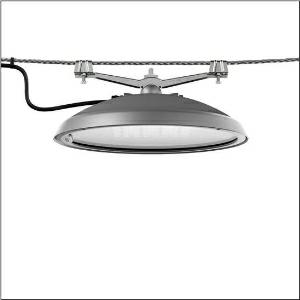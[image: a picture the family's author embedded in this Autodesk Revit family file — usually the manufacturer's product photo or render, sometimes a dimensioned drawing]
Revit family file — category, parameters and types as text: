
# Revit family: dl_r__50_iq_mini___p1_0s_5xa248u41f08fe_3d02
name_source: partatom
category: Lighting Fixtures
units: mm (PartAtom-declared; Revit-internal decimal feet)

## family parameters
Cut with Voids When Loaded = No
Host = Face
Light Source = No
Part Type = Normal
Room Calculation Point = No
Round Connector Dimension = Use Diameter
Shared = No

## types (1)
- --- (1 x LED, 2610 lm, 15.7 W, 4000K)
    Apparent Load = 16 VA
    CIE Flux Codes = 23 54 93 100 100
    Color Rendering = 70
    Color Temperature = 4000K
    Default Elevation = 1800 mm
    Description = DL® 50 iQ mini, catenary luminaire, primary light control with lens, of PMMA, primary optical cover: cover, of toughened safety glass, transparent, light distribution: P1.0s, light emission: direct distribution, primary light characteristic: symmetric, installation type: suspended mounting, LED, High Power LED, rated luminous flux: 2.610lm, luminous efficacy: 166lm/W, light colour: 740, colour temperature: 4000K, control gear: iQ Street-Remote, control: optimised constant luminous flux control (CLO 2.0), Desk-Remote (wireless, voltage-free reading and setting of iQ features in the workshop via application-optimized NFC function/RFID function), Light-Fading, Smart-Wire, Night-Set, Lumen-Switch, Temp-Guard, Auto-Match, Street-Remote, mains connection: 230..240V, AC, 50/60Hz, start of lifetime: 16W, end of service life: 16W, reduction: 8W, luminaire housing, of diecast aluminium, powder-coated, Siteco® metallic grey (DB 702S), diameter: 500mm, height: 115mm, mounting height: 4..12m, protection rating (complete): IP66, insulation class (complete): insulation class II (safety insulation), certification: CE, ENEC, ENEC+, VDE, impact resistance: IK08, permissible operating ambient temperature for outdoor applications: -25..+40°C, standard-compliant lighting for roads and squares, packaging unit: 1 piece

Light Distribution: P1.0s
    Height = 124 mm  [stored 0.406824 ft]
    Lamp = 1 x LED
    Lamp Light Flux = 2610 lm
    Lamp Power = 15.7 W
    Lamp count = 1
    Length = 500 mm
    Luminous efficacy = 166 lm/W
    Manufacturer = Siteco
    ModVariant = No
    Model = 5XA248U41F08FE
    Number of Poles = 1
    OnlyDefault = Yes
    Power Factor = 1
    Product Name = DL® 50 iQ mini | P1.0s
    Product group = catenary luminaire
    ProductGroupID = 6300
    Protection Class = Protection class II
    Protection Degree = IP 66
    RLX_Detail_Level = 1
    RLX_Emergency_Light_Flux = 0 lm
    RLX_Emergency_Type = 0
    RLX_Emergency_Type_DB = No
    RlxData = <blob elided: 122833 chars, md5=f496210c>
    Socket = socket
    Standby Power = 0 W
    System Light Flux = 2610 lm
    System Power = 16 W
    Type Comments = factory setting: luminous flux: 100 % | dim-lin: 254 | 319 mA
    Type Image = l_1242791.jpg
    URL = http://relux.com
    VarID = @adj_137760
    Voltage = 0 V
    Weight = 0.00 kg
    Width = 0 mm  [stored 0 ft]

note: [stored X ft] marks values corroborated as IEEE doubles in the binary element streams (Revit-internal decimal feet)

## geometry (parser evidence)
native form markers: Blend x4, Sweep x14
no freeform markers — native parametric forms only
